# Revit family: Pisa table
name_source: partatom
category: Furniture
revit_build: Autodesk Revit 2015 (Build: 20140606_1530(x64)
units: mm (PartAtom-declared; Revit-internal decimal feet)

## types (20) — shared parameters
Chrome = Chrome
Manufacturer = Isku Oy
Studs material = Rubber
Table top material = White laminate
Type Comments = Available as antimicrobial
URL = www.isku.fi

## per-type parameters (varying)
| type | Butterfly leg visibility | Lecture table legs visibility | Rectangular table top visibility | Round Table top visibility | Round table 1100mm legs visibility | Round table 900mm legs visibility | Round table leg position | Round table radius | Table depth | Table height | Table support | Table top thickness | Table width | Universal table legs vibility |
| Pisa 1401 general-purpose table 800x1200 | Yes | No | Yes | No | No | No | 116 mm | 900 mm  [stored 2.95276 ft] | 800 mm  [stored 2.62467 ft] | 730 mm  [stored 2.39501 ft] | 1142 mm | 24 mm  [stored 0.0787402 ft] | 1200 mm | No |
| Pisa 1401 general-purpose table 800x1600 | Yes | No | Yes | No | No | No | 116 mm | 900 mm  [stored 2.95276 ft] | 800 mm  [stored 2.62467 ft] | 730 mm  [stored 2.39501 ft] | 1542 mm  [stored 5.05906 ft] | 24 mm  [stored 0.0787402 ft] | 1600 mm  [stored 5.24934 ft] | No |
| Pisa 1401 general-purpose table 800x1800 | Yes | No | Yes | No | No | No | 116 mm | 900 mm  [stored 2.95276 ft] | 800 mm  [stored 2.62467 ft] | 730 mm  [stored 2.39501 ft] | 1742 mm  [stored 5.71522 ft] | 24 mm  [stored 0.0787402 ft] | 1800 mm  [stored 5.90551 ft] | No |
| Pisa 1401 general-purpose table 800x2000 | Yes | No | Yes | No | No | No | 116 mm | 900 mm  [stored 2.95276 ft] | 800 mm  [stored 2.62467 ft] | 730 mm  [stored 2.39501 ft] | 1942 mm  [stored 6.37139 ft] | 24 mm  [stored 0.0787402 ft] | 2000 mm  [stored 6.56168 ft] | No |
| Pisa 1401 general-purpose table 700x1200 | Yes | No | Yes | No | No | No | 116 mm | 900 mm  [stored 2.95276 ft] | 700 mm  [stored 2.29659 ft] | 730 mm  [stored 2.39501 ft] | 1142 mm | 24 mm  [stored 0.0787402 ft] | 1200 mm | No |
| Pisa 1401 general-purpose table 700x1600 | Yes | No | Yes | No | No | No | 116 mm | 900 mm  [stored 2.95276 ft] | 700 mm  [stored 2.29659 ft] | 730 mm  [stored 2.39501 ft] | 1542 mm  [stored 5.05906 ft] | 24 mm  [stored 0.0787402 ft] | 1600 mm  [stored 5.24934 ft] | No |
| Pisa 1401 general-purpose table 700x1800 | Yes | No | Yes | No | No | No | 116 mm | 900 mm  [stored 2.95276 ft] | 700 mm  [stored 2.29659 ft] | 730 mm  [stored 2.39501 ft] | 1742 mm  [stored 5.71522 ft] | 24 mm  [stored 0.0787402 ft] | 1800 mm  [stored 5.90551 ft] | No |
| Pisa 1402 lecture table 450x600 | No | Yes | Yes | No | No | No | 116 mm | 600 mm | 450 mm  [stored 1.47638 ft] | 726 mm | 542 mm  [stored 1.77822 ft] | 22 mm | 600 mm | No |
| Pisa 1402 lecture table 450x1200 | No | Yes | Yes | No | No | No | 116 mm | 900 mm  [stored 2.95276 ft] | 450 mm  [stored 1.47638 ft] | 726 mm | 1142 mm | 22 mm | 1200 mm | No |
| Pisa 1402 lecture table 500x700 | No | Yes | Yes | No | No | No | 116 mm | 625 mm | 500 mm  [stored 1.64042 ft] | 726 mm | 642 mm | 22 mm | 700 mm  [stored 2.29659 ft] | No |
| Pisa 1402 lecture table 500x1300 | No | Yes | Yes | No | No | No | 116 mm | 625 mm | 500 mm  [stored 1.64042 ft] | 726 mm | 1242 mm  [stored 4.0748 ft] | 22 mm | 1300 mm  [stored 4.26509 ft] | No |
| Pisa 1401 general-purpose table O11 | No | No | No | Yes | Yes | No | 170 mm  [stored 0.557743 ft] | 550 mm | 450 mm  [stored 1.47638 ft] | 726 mm | 1142 mm | 22 mm | 1200 mm | No |
| Pisa 1401 general-purpose table O9 | No | No | No | Yes | No | Yes | 115 mm  [stored 0.377297 ft] | 450 mm  [stored 1.47638 ft] | 450 mm  [stored 1.47638 ft] | 726 mm | 1142 mm | 22 mm | 1200 mm | No |
| Pisa 1400 general-purpose table 700x1200 | No | No | Yes | No | No | No | 116 mm | 900 mm  [stored 2.95276 ft] | 700 mm  [stored 2.29659 ft] | 722 mm  [stored 2.36877 ft] | 1142 mm | 22 mm | 1200 mm | Yes |
| Pisa 1400 general-purpose table 700x1600 | No | No | Yes | No | No | No | 116 mm | 900 mm  [stored 2.95276 ft] | 700 mm  [stored 2.29659 ft] | 722 mm  [stored 2.36877 ft] | 1542 mm  [stored 5.05906 ft] | 22 mm | 1600 mm  [stored 5.24934 ft] | Yes |
| Pisa 1400 general-purpose table 700x1800 | No | No | Yes | No | No | No | 116 mm | 900 mm  [stored 2.95276 ft] | 700 mm  [stored 2.29659 ft] | 722 mm  [stored 2.36877 ft] | 1742 mm  [stored 5.71522 ft] | 22 mm | 1800 mm  [stored 5.90551 ft] | Yes |
| Pisa 1400 general-purpose table 800x1200 | No | No | Yes | No | No | No | 116 mm | 900 mm  [stored 2.95276 ft] | 800 mm  [stored 2.62467 ft] | 722 mm  [stored 2.36877 ft] | 1142 mm | 22 mm | 1200 mm | Yes |
| Pisa 1400 general-purpose table 800x1600 | No | No | Yes | No | No | No | 116 mm | 900 mm  [stored 2.95276 ft] | 800 mm  [stored 2.62467 ft] | 722 mm  [stored 2.36877 ft] | 1542 mm  [stored 5.05906 ft] | 22 mm | 1600 mm  [stored 5.24934 ft] | Yes |
| Pisa 1400 general-purpose table 800x1800 | No | No | Yes | No | No | No | 116 mm | 900 mm  [stored 2.95276 ft] | 800 mm  [stored 2.62467 ft] | 722 mm  [stored 2.36877 ft] | 1742 mm  [stored 5.71522 ft] | 22 mm | 1800 mm  [stored 5.90551 ft] | Yes |
| Pisa 1400 general-purpose table 800x2000 | No | No | Yes | No | No | No | 116 mm | 900 mm  [stored 2.95276 ft] | 800 mm  [stored 2.62467 ft] | 722 mm  [stored 2.36877 ft] | 1942 mm  [stored 6.37139 ft] | 22 mm | 2000 mm  [stored 6.56168 ft] | Yes |

note: [stored X ft] marks values corroborated as IEEE doubles in the binary element streams (Revit-internal decimal feet)

## geometry (parser evidence)
native form markers: Sweep x32
no freeform markers — native parametric forms only
